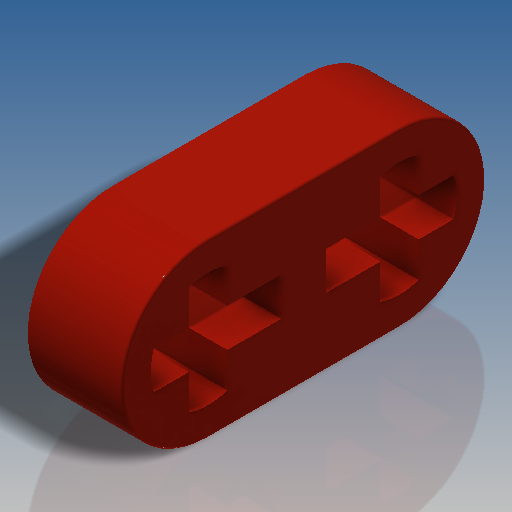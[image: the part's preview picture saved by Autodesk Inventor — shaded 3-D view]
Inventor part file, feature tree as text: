
AUTODESK INVENTOR PART (.ipt)
format: ipt  version: 2018.3 (Build 223284000, 284)  size: 209,920 bytes
history: native  units: mm
features: extrude x1, fillet x1, sketch x1
ambient origin geometry x8: Origin, YZ Plane, XZ Plane, XY Plane, X Axis, Y Axis, Z Axis, Center Point
bodies: Solid1 (feature_tree)
feature tree (3):
  extrude  "Extrusion4"  Depth=7.2mm
  fillet  "Fillet1"  Radius=1.6mm
  sketch  "Sketch3"  dims[d15=4.0mm d16=0.0mm d47=4.8mm d49=7.2mm d53=1.6mm d56=0.1mm d57=0.8mm d58=8.0mm]
